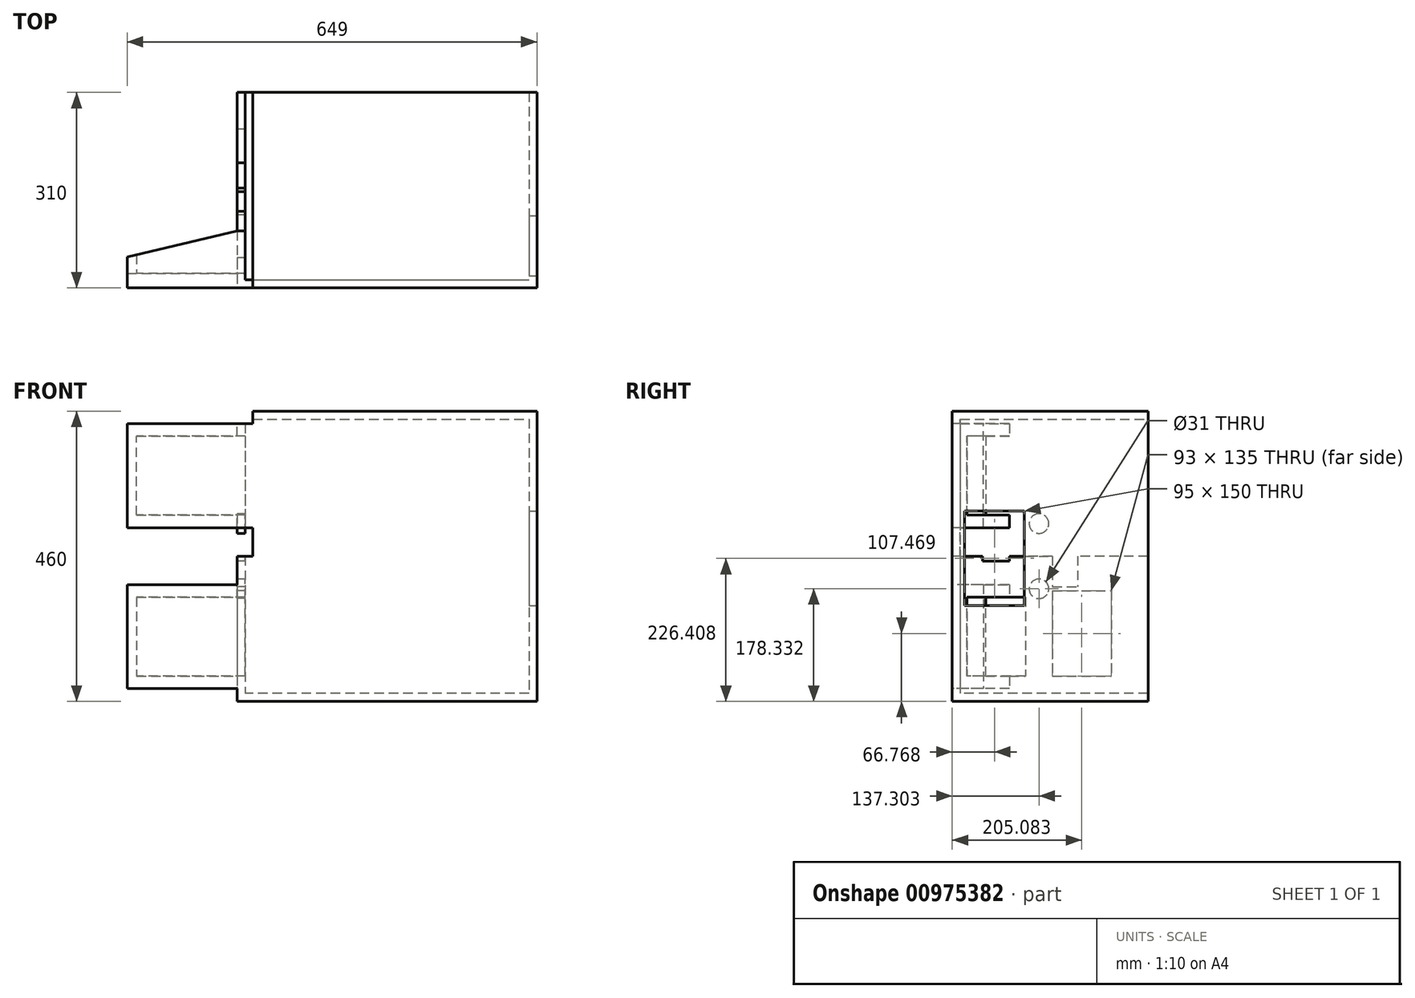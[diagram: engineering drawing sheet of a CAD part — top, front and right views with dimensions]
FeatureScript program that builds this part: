
annotation { "Feature Type Name" : "Feature", "Feature Type Description" : "" }
export const myFeature = defineFeature(function(context is Context, id is Id, definition is map)
    precondition{}
    {
        {
            var Q0;
            Q0=qCreatedBy(makeId("Top.planeOp"),FACE);
            var sketch = newSketch(context, id + "F0", { "sketchPlane" : qUnion([Q0])});
            skLineSegment(sketch, "E0.bottom", {"start": v(-237.5, 155) * mm, "end": v(237.5, 155) * mm});
            skLineSegment(sketch, "E0.top", {"start": v(-237.5, -155) * mm, "end": v(237.5, -155) * mm});
            skLineSegment(sketch, "E0.left", {"start": v(-237.5, 155) * mm, "end": v(-237.5, -155) * mm});
            skLineSegment(sketch, "E0.right", {"start": v(237.5, 155) * mm, "end": v(237.5, -155) * mm});
            skPoint(sketch, "E0.middle", {"position": v(0, 0) * mm});
            skSolve(sketch);
        }
        {
            var Q0;
            Q0 = qSketchRegion(id + "F0", true);
            extrude(context, id + "F1", {"entities" : qUnion([Q0]), "endBound" : BoundingType.SYMMETRIC, "depth" : 230 * mm, "offsetDistance" : 25 * mm});
        }
        {
            var Q0;
            Q0=makeQuery(id+"F1.opExtrude","CAP_FACE",FACE,{"disambiguationData":[OSD([sQuery(id+"F0.wireOp",EDGE,"E0.bottom"),sQuery(id+"F0.wireOp",EDGE,"E0.top"),sQuery(id+"F0.wireOp",EDGE,"E0.left"),sQuery(id+"F0.wireOp",EDGE,"E0.right")])],"isStart":false});
            shell(context, id + "F2", {"entities" : qUnion([Q0]), "thickness" : 12.7 * mm});
        }
        {
            var Q0;
            Q0=makeQuery(id+"F1.opExtrude","SWEPT_FACE",FACE,{"disambiguationData":[OSD([sQuery(id+"F0.wireOp",EDGE,"E0.left")])]});
            var sketch = newSketch(context, id + "F3", { "sketchPlane" : qUnion([Q0])});
            skLineSegment(sketch, "E1.bottom", {"start": v(131.98, 49.97) * mm, "end": v(38.98, 49.97) * mm});
            skLineSegment(sketch, "E1.top", {"start": v(131.98, -75.03) * mm, "end": v(38.98, -75.03) * mm});
            skLineSegment(sketch, "E1.left", {"start": v(131.98, 49.97) * mm, "end": v(131.98, -75.03) * mm});
            skLineSegment(sketch, "E1.right", {"start": v(38.98, 49.97) * mm, "end": v(38.98, -75.03) * mm});
            skPoint(sketch, "E2.left.start.orphan", {"position": v(0, 49.97) * mm});
            skPoint(sketch, "E2.right.end.orphan", {"position": v(-87.86, -75.03) * mm});
            skLineSegment(sketch, "E3.bottom", {"start": v(-3.58, 59.97) * mm, "end": v(-96.58, 59.97) * mm});
            skLineSegment(sketch, "E3.top", {"start": v(-3.58, -75.03) * mm, "end": v(-96.58, -75.03) * mm});
            skLineSegment(sketch, "E3.left", {"start": v(-3.58, 59.97) * mm, "end": v(-3.58, -75.03) * mm});
            skLineSegment(sketch, "E3.right", {"start": v(-96.58, 59.97) * mm, "end": v(-96.58, -75.03) * mm});
            skSolve(sketch);
        }
        {
            var Q0;
            Q0=makeQuery(id+"F3.imprint","IMPRINT",FACE,{"disambiguationData":[TD([[makeQuery(id+"F3.imprint","IMPRINT",EDGE,{"derivedFrom":sQuery(id+"F3.wireOp",EDGE,"E1.bottom")}),1.0]])]});
            var Q1;
            Q1=makeQuery(id+"F3.imprint","IMPRINT",FACE,{"disambiguationData":[TD([[makeQuery(id+"F3.imprint","IMPRINT",EDGE,{"derivedFrom":sQuery(id+"F3.wireOp",EDGE,"E2.bottom")}),1.0]])]});
            var Q2;
            Q2=makeQuery(id+"F3.imprint","IMPRINT",FACE,{"disambiguationData":[TD([[makeQuery(id+"F3.imprint","IMPRINT",EDGE,{"derivedFrom":sQuery(id+"F3.wireOp",EDGE,"E3.bottom")}),1.0]])]});
            extrude(context, id + "F4", {"entities" : qUnion([Q0, Q1, Q2]), "operationType" : NewBodyOperationType.REMOVE, "oppositeDirection" : true, "depth" : 25 * mm, "offsetDistance" : 25 * mm});
        }
        {
            var Q0;
            Q0=makeQuery(id+"F2.opShell","OFFSET_FACE",FACE,{"disambiguationData":[OSD([sQuery(id+"F0.wireOp",EDGE,"E0.bottom")])]});
            extrude(context, id + "F5", {"entities" : qUnion([Q0]), "operationType" : NewBodyOperationType.REMOVE, "oppositeDirection" : true, "depth" : 25 * mm, "offsetDistance" : 25 * mm});
        }
        {
            var Q0;
            Q0=makeQuery(id+"F1.opExtrude","SWEPT_FACE",FACE,{"disambiguationData":[OSD([sQuery(id+"F0.wireOp",EDGE,"E0.left")])]});
            var sketch = newSketch(context, id + "F6", { "sketchPlane" : qUnion([Q0])});
            skLineSegment(sketch, "E4.bottom", {"start": v(38.98, -75.03) * mm, "end": v(131.98, -75.03) * mm});
            skLineSegment(sketch, "E4.top", {"start": v(38.98, -95.03) * mm, "end": v(131.98, -95.03) * mm});
            skLineSegment(sketch, "E4.left", {"start": v(38.98, -75.03) * mm, "end": v(38.98, -95.03) * mm});
            skLineSegment(sketch, "E5.bottom", {"start": v(38.98, 49.97) * mm, "end": v(131.98, 49.97) * mm});
            skLineSegment(sketch, "E5.top", {"start": v(38.98, 69.97) * mm, "end": v(131.98, 69.97) * mm});
            skLineSegment(sketch, "E5.left", {"start": v(38.98, 49.97) * mm, "end": v(38.98, 69.97) * mm});
            skLineSegment(sketch, "E5.right", {"start": v(131.98, 69.9) * mm, "end": v(131.98, 69.97) * mm});
            skLineSegment(sketch, "E6.bottom", {"start": v(131.98, -95.03) * mm, "end": v(155, -95.03) * mm});
            skLineSegment(sketch, "E6.top", {"start": v(131.98, 69.9) * mm, "end": v(155, 69.9) * mm});
            skLineSegment(sketch, "E6.left", {"start": v(131.98, -75.03) * mm, "end": v(131.98, 49.97) * mm});
            skLineSegment(sketch, "E6.right", {"start": v(155, -95.03) * mm, "end": v(155, 69.9) * mm});
            skLineSegment(sketch, "E7", {"start": v(-155, 115) * mm, "end": v(155, 115) * mm});
            skSolve(sketch);
        }
        {
            var Q0;
            Q0=makeQuery(id+"F6.imprint","IMPRINT",FACE,{"disambiguationData":[TD([[makeQuery(id+"F6.imprint","IMPRINT",EDGE,{"derivedFrom":sQuery(id+"F6.wireOp",EDGE,"E4.bottom")}),1.0]])]});
            extrude(context, id + "F7", {"entities" : qUnion([Q0]), "operationType" : NewBodyOperationType.ADD, "depth" : 174 * mm, "offsetDistance" : 25 * mm});
        }
        {
            var Q0;
            Q0=makeQuery(id+"F7.boolean.opBoolean","MERGE",FACE,{"derivedFrom":[makeQuery(id+"F4.boolean.opBoolean","COPY",FACE,{"derivedFrom":makeQuery(id+"F4.opExtrude","SWEPT_FACE",FACE,{"disambiguationData":[OSD([sQuery(id+"F3.wireOp",EDGE,"E1.left")])]})}),makeQuery(id+"F7.opExtrude","SWEPT_FACE",FACE,{"disambiguationData":[OSD([sQuery(id+"F6.wireOp",EDGE,"E6.left")])]})]});
            var sketch = newSketch(context, id + "F8", { "sketchPlane" : qUnion([Q0])});
            skLineSegment(sketch, "E8.bottom", {"start": v(411.5, 49.97) * mm, "end": v(396.5, 49.97) * mm});
            skLineSegment(sketch, "E8.top", {"start": v(411.5, -75.03) * mm, "end": v(396.5, -75.03) * mm});
            skLineSegment(sketch, "E8.left", {"start": v(411.5, 49.97) * mm, "end": v(411.5, -75.03) * mm});
            skLineSegment(sketch, "E8.right", {"start": v(396.5, 49.97) * mm, "end": v(396.5, -75.03) * mm});
            skSolve(sketch);
        }
        {
            var Q0;
            Q0=makeQuery(id+"F7.opExtrude","SWEPT_FACE",FACE,{"disambiguationData":[OSD([sQuery(id+"F6.wireOp",EDGE,"E4.top"),sQuery(id+"F6.wireOp",EDGE,"E6.bottom")])]});
            var sketch = newSketch(context, id + "F9", { "sketchPlane" : qUnion([Q0])});
            skLineSegment(sketch, "E9", {"start": v(-237.5, 38.98) * mm, "end": v(-237.5, 64.54) * mm});
            skLineSegment(sketch, "E10", {"start": v(-237.5, 64.54) * mm, "end": v(-411.5, 105.77) * mm});
            skLineSegment(sketch, "E11", {"start": v(-411.5, 105.77) * mm, "end": v(-411.5, 38.98) * mm});
            skLineSegment(sketch, "E12", {"start": v(-411.5, 38.98) * mm, "end": v(-237.5, 38.98) * mm});
            skSolve(sketch);
        }
        {
            var Q0;
            Q0 = qSketchRegion(id + "F8", true);
            extrude(context, id + "F10", {"entities" : qUnion([Q0]), "operationType" : NewBodyOperationType.ADD, "depth" : 35 * mm, "offsetDistance" : 25 * mm});
        }
        {
            var Q0;
            Q0=makeQuery(id+"F9.imprint","IMPRINT",FACE,{"disambiguationData":[TD([[makeQuery(id+"F9.imprint","IMPRINT",EDGE,{"derivedFrom":sQuery(id+"F9.wireOp",EDGE,"E9")}),1.0]])]});
            extrude(context, id + "F11", {"entities" : qUnion([Q0]), "operationType" : NewBodyOperationType.REMOVE, "oppositeDirection" : true, "depth" : 363 * mm, "offsetDistance" : 25 * mm});
        }
        {
            var Q0;
            Q0=makeQuery(id+"F1.opExtrude","SWEPT_BODY",BODY,{"disambiguationData":[OSD([sQuery(id+"F0.wireOp",EDGE,"E0.bottom"),sQuery(id+"F0.wireOp",EDGE,"E0.top"),sQuery(id+"F0.wireOp",EDGE,"E0.left"),sQuery(id+"F0.wireOp",EDGE,"E0.right")])]});
            var Q1;
            Q1=makeQuery(id+"F1.opExtrude","CAP_FACE",FACE,{"disambiguationData":[OSD([sQuery(id+"F0.wireOp",EDGE,"E0.bottom"),sQuery(id+"F0.wireOp",EDGE,"E0.top"),sQuery(id+"F0.wireOp",EDGE,"E0.left"),sQuery(id+"F0.wireOp",EDGE,"E0.right")])],"isStart":false});
            mirror(context, id + "F12", {"operationType" : NewBodyOperationType.ADD, "entities" : qUnion([Q0]), "mirrorPlane" : qUnion([Q1])});
        }
        {
            var Q0;
            {var subQ0=makeQuery(id+"F11.boolean.opBoolean","MERGE",FACE,{"derivedFrom":[makeQuery(id+"F1.opExtrude","SWEPT_FACE",FACE,{"disambiguationData":[OSD([sQuery(id+"F0.wireOp",EDGE,"E0.left")])]})],"fromTools":[makeQuery(id+"F11.opExtrude","SWEPT_FACE",FACE,{"disambiguationData":[OSD([sQuery(id+"F9.wireOp",EDGE,"E9")])]})]});Q0=makeQuery(id+"F12.boolean.opBoolean","MERGE",FACE,{"derivedFrom":[subQ0,makeQuery(id+"F12.opPattern","COPY",FACE,{"derivedFrom":subQ0,"instanceName":"1"})]});}
            var sketch = newSketch(context, id + "F13", { "sketchPlane" : qUnion([Q0])});
            skLineSegment(sketch, "E13.bottom", {"start": v(64.54, 122.9) * mm, "end": v(107.04, 122.9) * mm});
            skLineSegment(sketch, "E13.top", {"start": v(64.54, 106.9) * mm, "end": v(107.04, 106.9) * mm});
            skLineSegment(sketch, "E13.left", {"start": v(64.54, 122.9) * mm, "end": v(64.54, 106.9) * mm});
            skLineSegment(sketch, "E13.right", {"start": v(107.04, 122.9) * mm, "end": v(107.04, 106.9) * mm});
            skLineSegment(sketch, "E14.bottom", {"start": v(-3.58, 66.7) * mm, "end": v(-43.58, 66.7) * mm});
            skLineSegment(sketch, "E14.top", {"start": v(-3.58, 163.7) * mm, "end": v(-43.58, 163.7) * mm});
            skLineSegment(sketch, "E14.left", {"start": v(-3.58, 66.7) * mm, "end": v(-3.58, 163.7) * mm});
            skLineSegment(sketch, "E14.right", {"start": v(-43.58, 66.7) * mm, "end": v(-43.58, 163.7) * mm});
            skLineSegment(sketch, "E15", {"start": v(-3.58, 66.7) * mm, "end": v(-3.58, 59.97) * mm});
            skLineSegment(sketch, "E16", {"start": v(-3.58, 59.97) * mm, "end": v(-3.58, 63.33) * mm});
            skLineSegment(sketch, "E17", {"start": v(-3.58, 63.33) * mm, "end": v(38.98, 63.33) * mm});
            skLineSegment(sketch, "E18", {"start": v(17.7, 63.33) * mm, "end": v(38.98, 63.33) * mm});
            skCircle(sketch, "E19", {"center": v(17.7, 63.33) * mm, "radius": 15.5 * mm});
            skLineSegment(sketch, "E20", {"start": v(-155, 115) * mm, "end": v(155, 115) * mm});
            skCircle(sketch, "E21.MirrorC", {"center": v(17.7, 166.67) * mm, "radius": 15.5 * mm});
            skSolve(sketch);
        }
        {
            var Q0;
            Q0=makeQuery(id+"F13.imprint","IMPRINT",FACE,{"disambiguationData":[TD([[makeQuery(id+"F13.imprint","IMPRINT",EDGE,{"derivedFrom":sQuery(id+"F13.wireOp",EDGE,"E13.bottom")}),-1.0]])]});
            var Q1;
            Q1=makeQuery(id+"F13.imprint","IMPRINT",FACE,{"disambiguationData":[TD([[makeQuery(id+"F13.imprint","IMPRINT",EDGE,{"derivedFrom":sQuery(id+"F13.wireOp",EDGE,"E14.bottom")}),-1.0]])]});
            var Q2;
            {var subQ0=sQuery(id+"F13.wireOp",EDGE,"E14.top");Q2=makeQuery(id+"F13.imprint","IMPRINT",FACE,{"disambiguationData":[TD([[makeQuery(id+"F13.imprint","IMPRINT",EDGE,{"derivedFrom":subQ0}),1.0]])]});}
            var Q3;
            {var subQ0=sQuery(id+"F13.wireOp",EDGE,"E13.top");Q3=makeQuery(id+"F13.imprint","IMPRINT",FACE,{"disambiguationData":[TD([[makeQuery(id+"F13.imprint","IMPRINT",EDGE,{"derivedFrom":subQ0}),1.0]])]});}
            extrude(context, id + "F14", {"entities" : qUnion([Q0, Q1, Q2, Q3]), "operationType" : NewBodyOperationType.REMOVE, "oppositeDirection" : true, "depth" : 25 * mm, "offsetDistance" : 25 * mm});
        }
        {
            var Q0;
            {var subQ0=makeQuery(id+"F1.opExtrude","SWEPT_FACE",FACE,{"disambiguationData":[OSD([sQuery(id+"F0.wireOp",EDGE,"E0.right")])]});Q0=makeQuery(id+"F12.boolean.opBoolean","MERGE",FACE,{"derivedFrom":[subQ0,makeQuery(id+"F12.opPattern","COPY",FACE,{"derivedFrom":subQ0,"instanceName":"1"})]});}
            var sketch = newSketch(context, id + "F15", { "sketchPlane" : qUnion([Q0])});
            skLineSegment(sketch, "E22.bottom", {"start": v(-40.73, 186.4) * mm, "end": v(-135.73, 186.4) * mm});
            skLineSegment(sketch, "E22.top", {"start": v(-40.73, 36.4) * mm, "end": v(-135.73, 36.4) * mm});
            skLineSegment(sketch, "E22.left", {"start": v(-40.73, 186.4) * mm, "end": v(-40.73, 36.4) * mm});
            skLineSegment(sketch, "E22.right", {"start": v(-135.73, 186.4) * mm, "end": v(-135.73, 36.4) * mm});
            skSolve(sketch);
        }
        {
            var Q0;
            Q0=makeQuery(id+"F15.imprint","IMPRINT",FACE,{"disambiguationData":[TD([[makeQuery(id+"F15.imprint","IMPRINT",EDGE,{"derivedFrom":sQuery(id+"F15.wireOp",EDGE,"E22.bottom")}),1.0]])]});
            extrude(context, id + "F16", {"entities" : qUnion([Q0]), "operationType" : NewBodyOperationType.REMOVE, "oppositeDirection" : true, "depth" : 25 * mm, "offsetDistance" : 25 * mm});
        }
        {
            var Q0;
            Q0=makeQuery(id+"F13.imprint","IMPRINT",FACE,{"disambiguationData":[TD([[makeQuery(id+"F13.imprint","IMPRINT",EDGE,{"derivedFrom":sQuery(id+"F13.wireOp",EDGE,"E21.MirrorC")}),-1.0]])]});
            var Q1;
            {var subQ0=sQuery(id+"F13.wireOp",EDGE,"E18");var subQ1=sQuery(id+"F13.wireOp",EDGE,"E17");var subQ2=makeQuery(id+"F13.imprint","INTERSECT",VERTEX,{"derivedFrom":[subQ1,subQ0]});Q1=makeQuery(id+"F13.imprint","IMPRINT",FACE,{"disambiguationData":[TD([[makeQuery(id+"F13.imprint","IMPRINT",EDGE,{"disambiguationData":[TD([[subQ2,1.0]])],"derivedFrom":subQ1}),1.0]])]});}
            var Q2;
            {var subQ0=sQuery(id+"F13.wireOp",EDGE,"E18");var subQ1=sQuery(id+"F13.wireOp",EDGE,"E17");var subQ2=makeQuery(id+"F13.imprint","INTERSECT",VERTEX,{"derivedFrom":[subQ1,subQ0]});Q2=makeQuery(id+"F13.imprint","IMPRINT",FACE,{"disambiguationData":[TD([[makeQuery(id+"F13.imprint","IMPRINT",EDGE,{"disambiguationData":[TD([[subQ2,1.0]])],"derivedFrom":subQ1}),-1.0]])]});}
            extrude(context, id + "F17", {"entities" : qUnion([Q0, Q1, Q2]), "operationType" : NewBodyOperationType.REMOVE, "oppositeDirection" : true, "depth" : 25 * mm, "offsetDistance" : 25 * mm});
        }
    });
